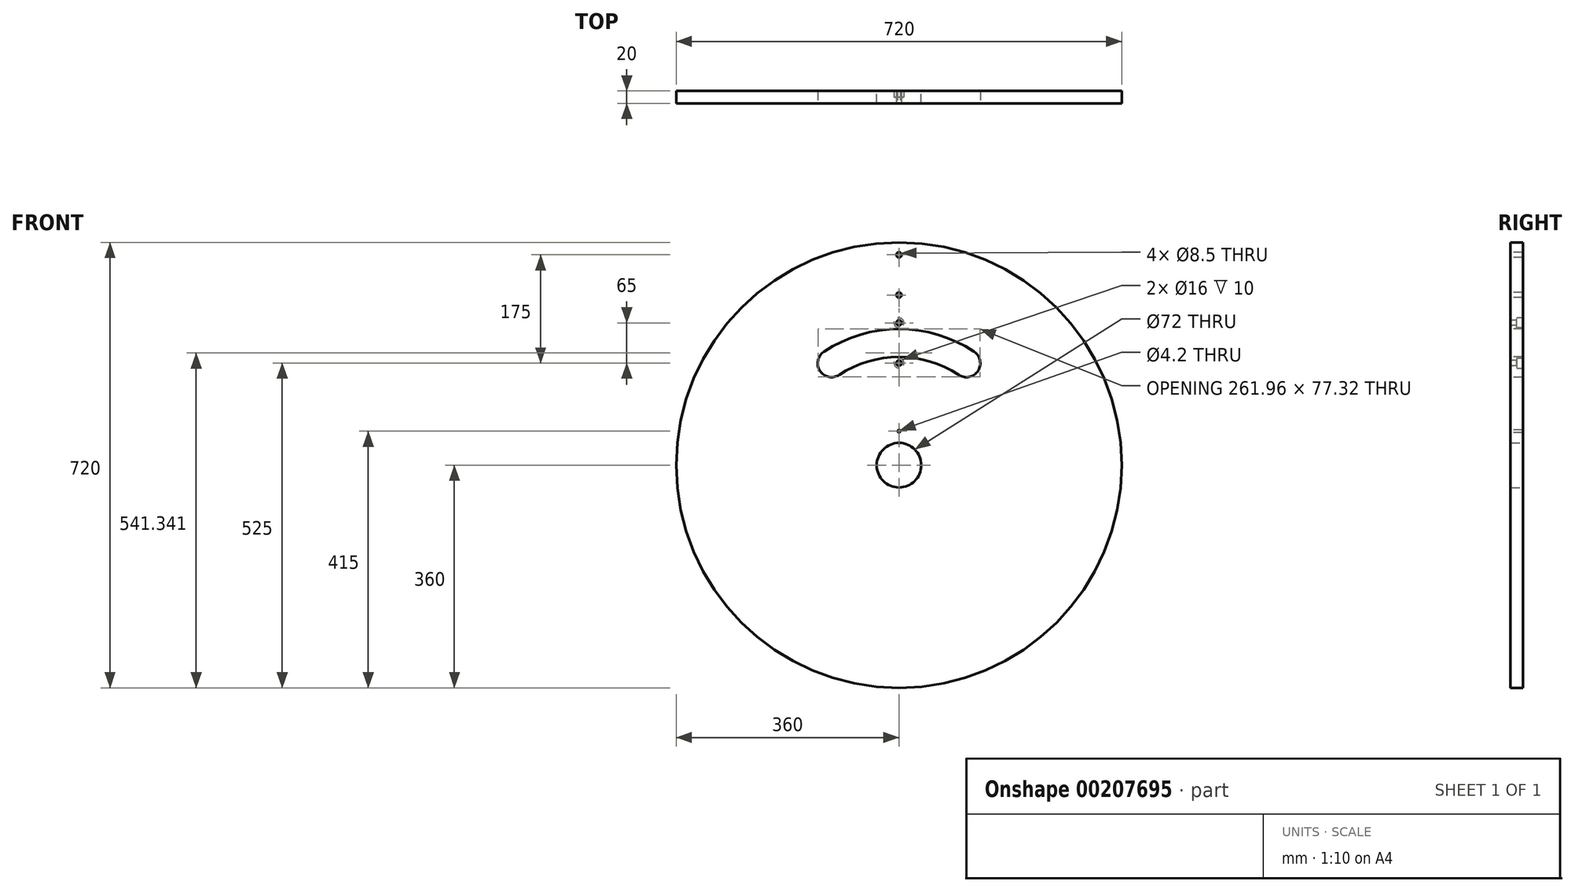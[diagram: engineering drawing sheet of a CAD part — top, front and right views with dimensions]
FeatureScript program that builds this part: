
annotation { "Feature Type Name" : "Feature", "Feature Type Description" : "" }
export const myFeature = defineFeature(function(context is Context, id is Id, definition is map)
    precondition{}
    {
        {
            var Q0;
            Q0=qCreatedBy(makeId("Front.planeOp"),FACE);
            var sketch = newSketch(context, id + "F0", { "sketchPlane" : qUnion([Q0])});
            skCircle(sketch, "E0", {"center": v(0, 0) * mm, "radius": 360 * mm});
            skCircle(sketch, "E1", {"center": v(0, 0) * mm, "radius": 36 * mm});
            skSolve(sketch);
        }
        {
            var Q0;
            Q0=makeQuery(id+"F0.imprint","IMPRINT",FACE,{"disambiguationData":[TD([[makeQuery(id+"F0.imprint","IMPRINT",EDGE,{"derivedFrom":sQuery(id+"F0.wireOp",EDGE,"E0")}),1.0]])]});
            extrude(context, id + "F1", {"entities" : qUnion([Q0]), "endBound" : BoundingType.SYMMETRIC, "depth" : 20 * mm});
        }
        {
            var Q0;
            Q0=makeQuery(id+"F1.opExtrude","CAP_FACE",FACE,{"disambiguationData":[OSD([sQuery(id+"F0.wireOp",EDGE,"E0"),sQuery(id+"F0.wireOp",EDGE,"E1")])],"isStart":false});
            var sketch = newSketch(context, id + "F2", { "sketchPlane" : qUnion([Q0])});
            skCircle(sketch, "E2", {"center": v(0, 165) * mm, "radius": 5 * mm});
            skCircle(sketch, "E3", {"center": v(0, 230) * mm, "radius": 5 * mm});
            skCircle(sketch, "E4", {"center": v(0, 340) * mm, "radius": 5 * mm});
            skSolve(sketch);
        }
        {
            var Q0;
            Q0=sQuery(id+"F2.wireOp",VERTEX,"E2.center");
            var Q1;
            Q1=sQuery(id+"F2.wireOp",VERTEX,"E3.center");
            var Q2;
            Q2=sQuery(id+"F2.wireOp",VERTEX,"E4.center");
            var Q3;
            Q3=makeQuery(id+"F1.opExtrude","SWEPT_BODY",BODY,{"disambiguationData":[OSD([sQuery(id+"F0.wireOp",EDGE,"E0"),sQuery(id+"F0.wireOp",EDGE,"E1")])]});
            hole(context, id + "F3", {"style" : HoleStyle.SIMPLE, "endStyle" : HoleEndStyle.BLIND, "standardTappedOrClearance" : lookupTablePath({ "standard" : "ISO", "engagement" : "75%", "pitch" : "1.5 mm", "size" : "M10", "type" : "Tapped" }), "standardBlindInLast" : lookupTablePath({ "standard" : "ISO", "engagement" : "75%", "pitch" : "1.5 mm", "size" : "M10", "type" : "Tapped" }), "holeDiameter" : 8.5 * mm, "showTappedDepth" : true, "holeDepth" : 30 * mm, "tappedDepth" : 25.5 * mm, "tapClearance" : 3, "locations" : qUnion([Q0, Q1, Q2]), "scope" : qUnion([Q3]), "majorDiameter" : 10 * mm});
        }
        {
            var Q0;
            Q0=makeQuery(id+"F1.opExtrude","CAP_FACE",FACE,{"disambiguationData":[OSD([sQuery(id+"F0.wireOp",EDGE,"E0"),sQuery(id+"F0.wireOp",EDGE,"E1")])],"isStart":false});
            var sketch = newSketch(context, id + "F4", { "sketchPlane" : qUnion([Q0])});
            skCircle(sketch, "E5", {"center": v(0, 0) * mm, "radius": 175 * mm});
            skCircle(sketch, "E6", {"center": v(0, 0) * mm, "radius": 220 * mm});
            skLineSegment(sketch, "E7", {"start": v(-141.41, 168.53) * mm, "end": v(0, 0) * mm});
            skLineSegment(sketch, "E8", {"start": v(0, 0) * mm, "end": v(141.41, 168.53) * mm});
            skCircle(sketch, "E9", {"center": v(-108.89, 164.77) * mm, "radius": 22.5 * mm});
            skCircle(sketch, "E10", {"center": v(108.89, 164.77) * mm, "radius": 22.5 * mm});
            skSolve(sketch);
        }
        {
            var Q0;
            {var subQ0=sQuery(id+"F4.wireOp",EDGE,"E10");var subQ1=sQuery(id+"F4.wireOp",EDGE,"E5");var subQ2=makeQuery(id+"F4.imprint","INTERSECT",VERTEX,{"derivedFrom":[subQ1,subQ0]});Q0=makeQuery(id+"F4.imprint","IMPRINT",FACE,{"disambiguationData":[TD([[makeQuery(id+"F4.imprint","IMPRINT",EDGE,{"disambiguationData":[TD([[subQ2,-1.0]])],"derivedFrom":subQ1}),-1.0]])]});}
            var Q1;
            {var subQ0=sQuery(id+"F4.wireOp",EDGE,"E9");var subQ1=makeQuery(id+"F4.imprint","INTERSECT",VERTEX,{"derivedFrom":[sQuery(id+"F4.wireOp",EDGE,"E6"),subQ0]});Q1=makeQuery(id+"F4.imprint","IMPRINT",FACE,{"disambiguationData":[TD([[makeQuery(id+"F4.imprint","IMPRINT",EDGE,{"disambiguationData":[TD([[subQ1,-1.0]])],"derivedFrom":subQ0}),1.0]])]});}
            var Q2;
            {var subQ0=sQuery(id+"F4.wireOp",EDGE,"E10");var subQ1=makeQuery(id+"F4.imprint","INTERSECT",VERTEX,{"derivedFrom":[sQuery(id+"F4.wireOp",EDGE,"E5"),subQ0]});Q2=makeQuery(id+"F4.imprint","IMPRINT",FACE,{"disambiguationData":[TD([[makeQuery(id+"F4.imprint","IMPRINT",EDGE,{"disambiguationData":[TD([[subQ1,1.0]])],"derivedFrom":subQ0}),1.0]])]});}
            extrude(context, id + "F5", {"entities" : qUnion([Q0, Q1, Q2]), "operationType" : NewBodyOperationType.REMOVE, "endBound" : BoundingType.THROUGH_ALL, "oppositeDirection" : true, "depth" : 25 * mm});
        }
        {
            var Q0;
            Q0=makeQuery(id+"F1.opExtrude","CAP_FACE",FACE,{"disambiguationData":[OSD([sQuery(id+"F0.wireOp",EDGE,"E0"),sQuery(id+"F0.wireOp",EDGE,"E1")])],"isStart":false});
            var sketch = newSketch(context, id + "F6", { "sketchPlane" : qUnion([Q0])});
            skCircle(sketch, "E11", {"center": v(0, 55) * mm, "radius": 2.5 * mm});
            skSolve(sketch);
        }
        {
            var Q0;
            Q0=sQuery(id+"F6.wireOp",VERTEX,"E11.center");
            var Q1;
            Q1=makeQuery(id+"F1.opExtrude","SWEPT_BODY",BODY,{"disambiguationData":[OSD([sQuery(id+"F0.wireOp",EDGE,"E0"),sQuery(id+"F0.wireOp",EDGE,"E1")])]});
            hole(context, id + "F7", {"style" : HoleStyle.SIMPLE, "endStyle" : HoleEndStyle.BLIND, "standardTappedOrClearance" : lookupTablePath({ "standard" : "ISO", "engagement" : "75%", "pitch" : "0.8 mm", "size" : "M5", "type" : "Tapped" }), "standardBlindInLast" : lookupTablePath({ "standard" : "ISO", "engagement" : "75%", "pitch" : "0.8 mm", "size" : "M5", "type" : "Tapped" }), "holeDiameter" : 4.2 * mm, "showTappedDepth" : true, "holeDepth" : 27.9 * mm, "tappedDepth" : 25.5 * mm, "tapClearance" : 3, "locations" : qUnion([Q0]), "scope" : qUnion([Q1]), "majorDiameter" : 5 * mm});
        }
        {
            var Q0;
            Q0=makeQuery(id+"F1.opExtrude","CAP_FACE",FACE,{"disambiguationData":[OSD([sQuery(id+"F0.wireOp",EDGE,"E0"),sQuery(id+"F0.wireOp",EDGE,"E1")])],"isStart":false});
            var sketch = newSketch(context, id + "F8", { "sketchPlane" : qUnion([Q0])});
            skCircle(sketch, "E12", {"center": v(0, 275) * mm, "radius": 5 * mm});
            skSolve(sketch);
        }
        {
            var Q0;
            Q0=sQuery(id+"F8.wireOp",VERTEX,"E12.center");
            var Q1;
            Q1=makeQuery(id+"F1.opExtrude","SWEPT_BODY",BODY,{"disambiguationData":[OSD([sQuery(id+"F0.wireOp",EDGE,"E0"),sQuery(id+"F0.wireOp",EDGE,"E1")])]});
            hole(context, id + "F9", {"style" : HoleStyle.SIMPLE, "endStyle" : HoleEndStyle.BLIND, "standardTappedOrClearance" : lookupTablePath({ "standard" : "ISO", "engagement" : "75%", "pitch" : "1.5 mm", "size" : "M10", "type" : "Tapped" }), "standardBlindInLast" : lookupTablePath({ "standard" : "ISO", "engagement" : "75%", "pitch" : "1.5 mm", "size" : "M10", "type" : "Tapped" }), "holeDiameter" : 8.5 * mm, "showTappedDepth" : true, "holeDepth" : 30 * mm, "tappedDepth" : 25.5 * mm, "tapClearance" : 3, "locations" : qUnion([Q0]), "scope" : qUnion([Q1]), "majorDiameter" : 10 * mm});
        }
        {
            var Q0;
            Q0=makeQuery(id+"F1.opExtrude","CAP_FACE",FACE,{"disambiguationData":[OSD([sQuery(id+"F0.wireOp",EDGE,"E0"),sQuery(id+"F0.wireOp",EDGE,"E1")])],"isStart":false});
            var sketch = newSketch(context, id + "F10", { "sketchPlane" : qUnion([Q0])});
            skCircle(sketch, "E13", {"center": v(0, 230) * mm, "radius": 8 * mm});
            skSolve(sketch);
        }
        {
            var Q0;
            Q0=makeQuery(id+"F10.imprint","IMPRINT",FACE,{"disambiguationData":[TD([[makeQuery(id+"F10.imprint","IMPRINT",EDGE,{"derivedFrom":makeQuery(id+"F3.hole-1.boolean.opBoolean","COPY",EDGE,{"derivedFrom":makeQuery(id+"F3.hole-1.opRevolve","SWEPT_EDGE",EDGE,{"disambiguationData":[OSD([sQuery(id+"F3.hole-1.sketch.wireOp",EDGE,"core_line_2"),sQuery(id+"F3.hole-1.sketch.wireOp",EDGE,"core_line_3")])]})})}),1.0]])]});
            var Q1;
            Q1=makeQuery(id+"F10.imprint","IMPRINT",FACE,{"disambiguationData":[TD([[makeQuery(id+"F10.imprint","IMPRINT",EDGE,{"derivedFrom":sQuery(id+"F10.wireOp",EDGE,"E13")}),1.0]])]});
            extrude(context, id + "F11", {"entities" : qUnion([Q0, Q1]), "operationType" : NewBodyOperationType.REMOVE, "oppositeDirection" : true, "depth" : 20 * mm, "hasSecondDirection" : true, "secondDirectionOppositeDirection" : true, "secondDirectionDepth" : 10 * mm});
        }
        {
            var Q0;
            Q0=makeQuery(id+"F1.opExtrude","CAP_FACE",FACE,{"disambiguationData":[OSD([sQuery(id+"F0.wireOp",EDGE,"E0"),sQuery(id+"F0.wireOp",EDGE,"E1")])],"isStart":true});
            var sketch = newSketch(context, id + "F12", { "sketchPlane" : qUnion([Q0])});
            skCircle(sketch, "E14", {"center": v(0, 165) * mm, "radius": 8 * mm});
            skSolve(sketch);
        }
        {
            var Q0;
            Q0=makeQuery(id+"F12.imprint","IMPRINT",FACE,{"disambiguationData":[TD([[makeQuery(id+"F12.imprint","IMPRINT",EDGE,{"derivedFrom":makeQuery(id+"F3.hole-0.boolean.opBoolean","INTERSECT",EDGE,{"derivedFrom":[makeQuery(id+"F1.opExtrude","CAP_FACE",FACE,{"disambiguationData":[OSD([sQuery(id+"F0.wireOp",EDGE,"E0"),sQuery(id+"F0.wireOp",EDGE,"E1")])],"isStart":true}),makeQuery(id+"F3.hole-0.opRevolve","SWEPT_FACE",FACE,{"disambiguationData":[OSD([sQuery(id+"F3.hole-0.sketch.wireOp",EDGE,"core_line_2")])]})]})}),1.0]])]});
            var Q1;
            Q1=makeQuery(id+"F12.imprint","IMPRINT",FACE,{"disambiguationData":[TD([[makeQuery(id+"F12.imprint","IMPRINT",EDGE,{"derivedFrom":sQuery(id+"F12.wireOp",EDGE,"E14")}),1.0]])]});
            extrude(context, id + "F13", {"entities" : qUnion([Q0, Q1]), "operationType" : NewBodyOperationType.REMOVE, "oppositeDirection" : true, "depth" : 10 * mm});
        }
    });
